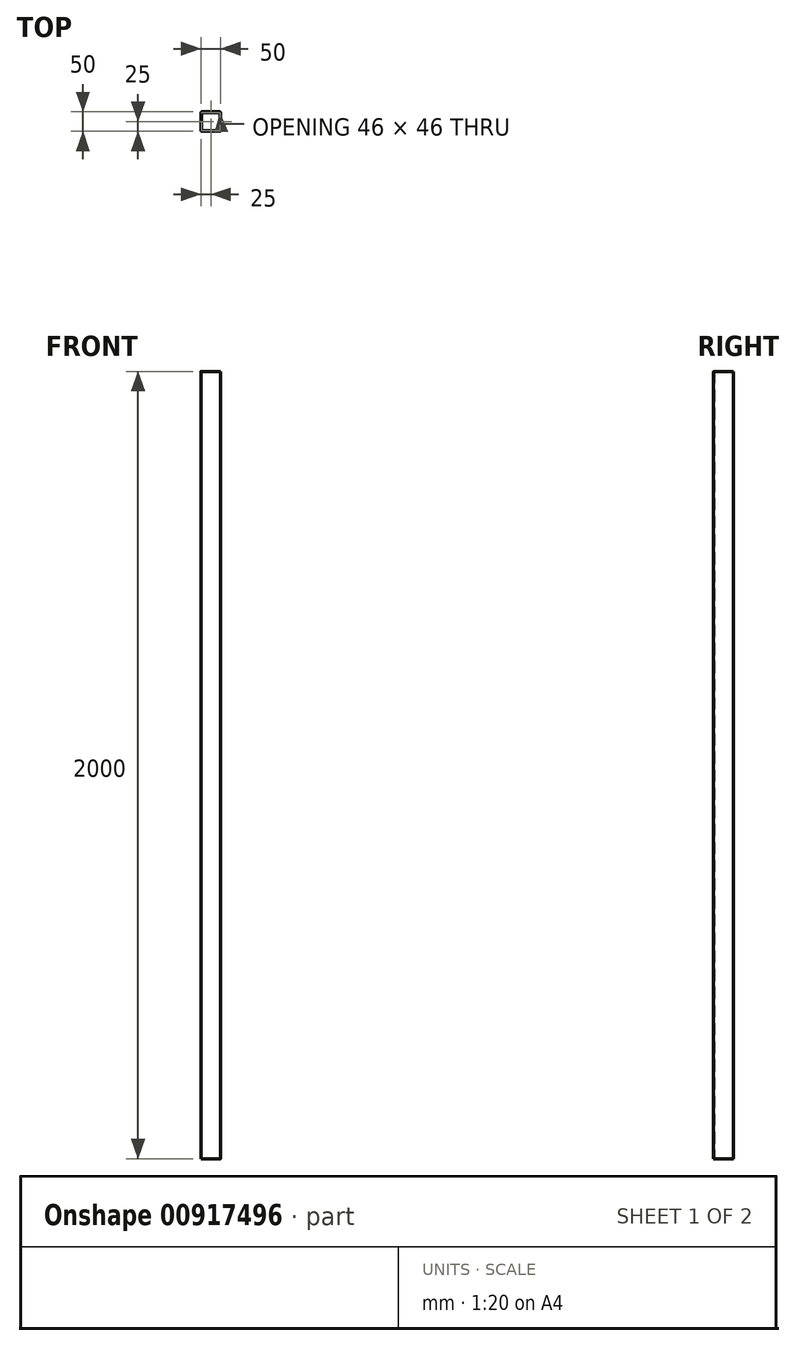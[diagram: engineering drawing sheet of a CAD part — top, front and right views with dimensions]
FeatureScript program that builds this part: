
annotation { "Feature Type Name" : "Feature", "Feature Type Description" : "" }
export const myFeature = defineFeature(function(context is Context, id is Id, definition is map)
    precondition{}
    {
        {
            var Q0;
            Q0=qCreatedBy(makeId("Top.planeOp"),FACE);
            var sketch = newSketch(context, id + "F0", { "sketchPlane" : qUnion([Q0])});
            skLineSegment(sketch, "E0.bottom", {"start": v(22, 25) * mm, "end": v(-22, 25) * mm});
            skLineSegment(sketch, "E0.top", {"start": v(22, -25) * mm, "end": v(-22, -25) * mm});
            skLineSegment(sketch, "E0.left", {"start": v(25, 22) * mm, "end": v(25, -22) * mm});
            skLineSegment(sketch, "E0.right", {"start": v(-25, 22) * mm, "end": v(-25, -22) * mm});
            skPoint(sketch, "E0.middle", {"position": v(0, 0) * mm});
            skPoint(sketch, "E1.visualSharp", {"position": v(-25, 25) * mm});
            skArc(sketch, "E1.filletArc", {"start": v(-22, 25) * mm, "mid": v(-24.12, 24.12) * mm, "end": v(-25, 22) * mm});
            skPoint(sketch, "E2.visualSharp", {"position": v(25, 25) * mm});
            skArc(sketch, "E2.filletArc", {"start": v(25, 22) * mm, "mid": v(24.12, 24.12) * mm, "end": v(22, 25) * mm});
            skPoint(sketch, "E3.visualSharp", {"position": v(25, -25) * mm});
            skArc(sketch, "E3.filletArc", {"start": v(22, -25) * mm, "mid": v(24.12, -24.12) * mm, "end": v(25, -22) * mm});
            skPoint(sketch, "E4.visualSharp", {"position": v(-25, -25) * mm});
            skArc(sketch, "E4.filletArc", {"start": v(-25, -22) * mm, "mid": v(-24.12, -24.12) * mm, "end": v(-22, -25) * mm});
            skLineSegment(sketch, "E5.0", {"start": v(22, -23) * mm, "end": v(-22, -23) * mm});
            skLineSegment(sketch, "E5.1", {"start": v(23, 23) * mm, "end": v(23, -22) * mm});
            skLineSegment(sketch, "E5.2", {"start": v(23, 23) * mm, "end": v(-22, 23) * mm});
            skLineSegment(sketch, "E5.3", {"start": v(-23, 22) * mm, "end": v(-23, -22) * mm});
            skPoint(sketch, "E6.visualSharp", {"position": v(-23, -23) * mm});
            skArc(sketch, "E6.filletArc", {"start": v(-23, -22) * mm, "mid": v(-22.7, -22.7) * mm, "end": v(-22, -23) * mm});
            skPoint(sketch, "E7.visualSharp", {"position": v(-23, 23) * mm});
            skArc(sketch, "E7.filletArc", {"start": v(-22, 23) * mm, "mid": v(-22.7, 22.7) * mm, "end": v(-23, 22) * mm});
            skPoint(sketch, "E8.visualSharp", {"position": v(23, -23) * mm});
            skArc(sketch, "E8.filletArc", {"start": v(22, -23) * mm, "mid": v(22.7, -22.7) * mm, "end": v(23, -22) * mm});
            skSolve(sketch);
        }
        {
            var Q0;
            Q0 = qSketchRegion(id + "F0", true);
            extrude(context, id + "F1", {"entities" : qUnion([Q0]), "depth" : 2000 * mm, "offsetDistance" : 25 * mm});
        }
    });
